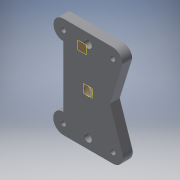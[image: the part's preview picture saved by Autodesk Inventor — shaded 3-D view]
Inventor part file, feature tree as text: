
AUTODESK INVENTOR PART (.ipt)
format: ipt  version: 2016 (Build 200138000, 138)  size: 221,696 bytes
history: native  units: in
note: dims shown in document units (in); Inventor stores cm internally (conversion verified against a paired STEP export)
features: extrude x4, sketch x4, reference x4, plane x2, projected_geometry x2
ambient origin geometry x8: Origin, YZ Plane, XZ Plane, XY Plane, X Axis, Y Axis, Z Axis, Center Point
bodies: Solid1 (feature_tree)
feature tree (16):
  plane  "Work Plane1"
  plane  "Work Plane2"
  extrude  "Extrusion1"  Depth=1.0in
  extrude  "Extrusion2"  Depth=0.2in
  extrude  "Extrusion3"  Depth=1.0in
  extrude  "Extrusion4"  Depth=0.2559in
  sketch  "Sketch1"  dims[d0=0.2in d1=1.0in]
  reference  "Reference1"
  reference  "Reference2"
  reference  "Reference3"
  sketch  "Sketch2"  dims[d2=0.2in d3=0.2in]
  projected_geometry  "Projected Loop1"
  sketch  "Sketch3"  dims[d4=0.2in d5=1.0in]
  sketch  "Sketch4"  dims[d6=0.3937in d7=0.0in d8=0.8661in d9=0.315in d10=0.0in d11=0.3937in d12=0.315in d13=0.0in d14=0.2in d15=0.2in d16=0.2in d17=0.2in d18=0.2in d19=0.2in d20=0.2in d21=0.2559in d22=0.0in]
  projected_geometry  "Projected Loop2"
  reference  "Reference4"
